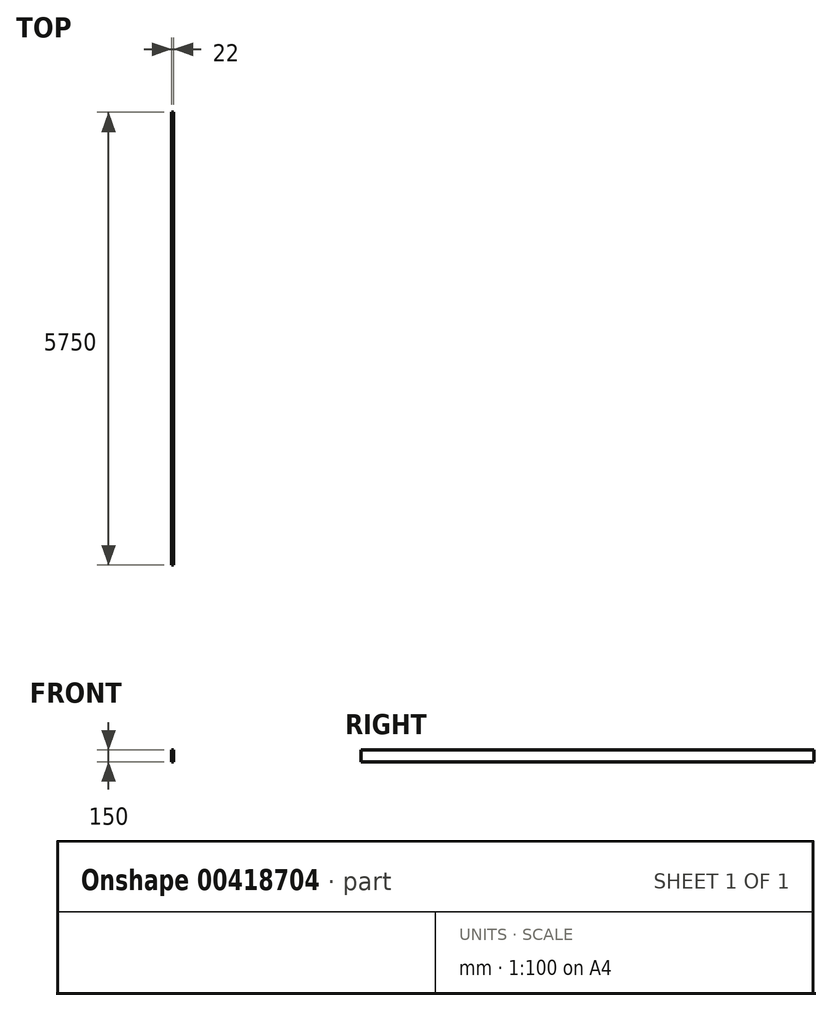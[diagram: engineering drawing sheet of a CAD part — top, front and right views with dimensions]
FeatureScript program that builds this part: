
annotation { "Feature Type Name" : "Feature", "Feature Type Description" : "" }
export const myFeature = defineFeature(function(context is Context, id is Id, definition is map)
    precondition{}
    {
        {
            var Q0;
            Q0=qCreatedBy(makeId("Front.planeOp"),FACE);
            var sketch = newSketch(context, id + "F0", { "sketchPlane" : qUnion([Q0])});
            skLineSegment(sketch, "E0.bottom", {"start": v(11, 75) * mm, "end": v(-11, 75) * mm});
            skLineSegment(sketch, "E0.top", {"start": v(11, -75) * mm, "end": v(-11, -75) * mm});
            skLineSegment(sketch, "E0.left", {"start": v(11, 75) * mm, "end": v(11, -75) * mm});
            skLineSegment(sketch, "E0.right", {"start": v(-11, 75) * mm, "end": v(-11, -75) * mm});
            skPoint(sketch, "E0.middle", {"position": v(0, 0) * mm});
            skSolve(sketch);
        }
        {
            var Q0;
            Q0 = qSketchRegion(id + "F0", true);
            extrude(context, id + "F1", {"entities" : qUnion([Q0]), "endBound" : BoundingType.SYMMETRIC, "depth" : 5750 * mm});
        }
    });
